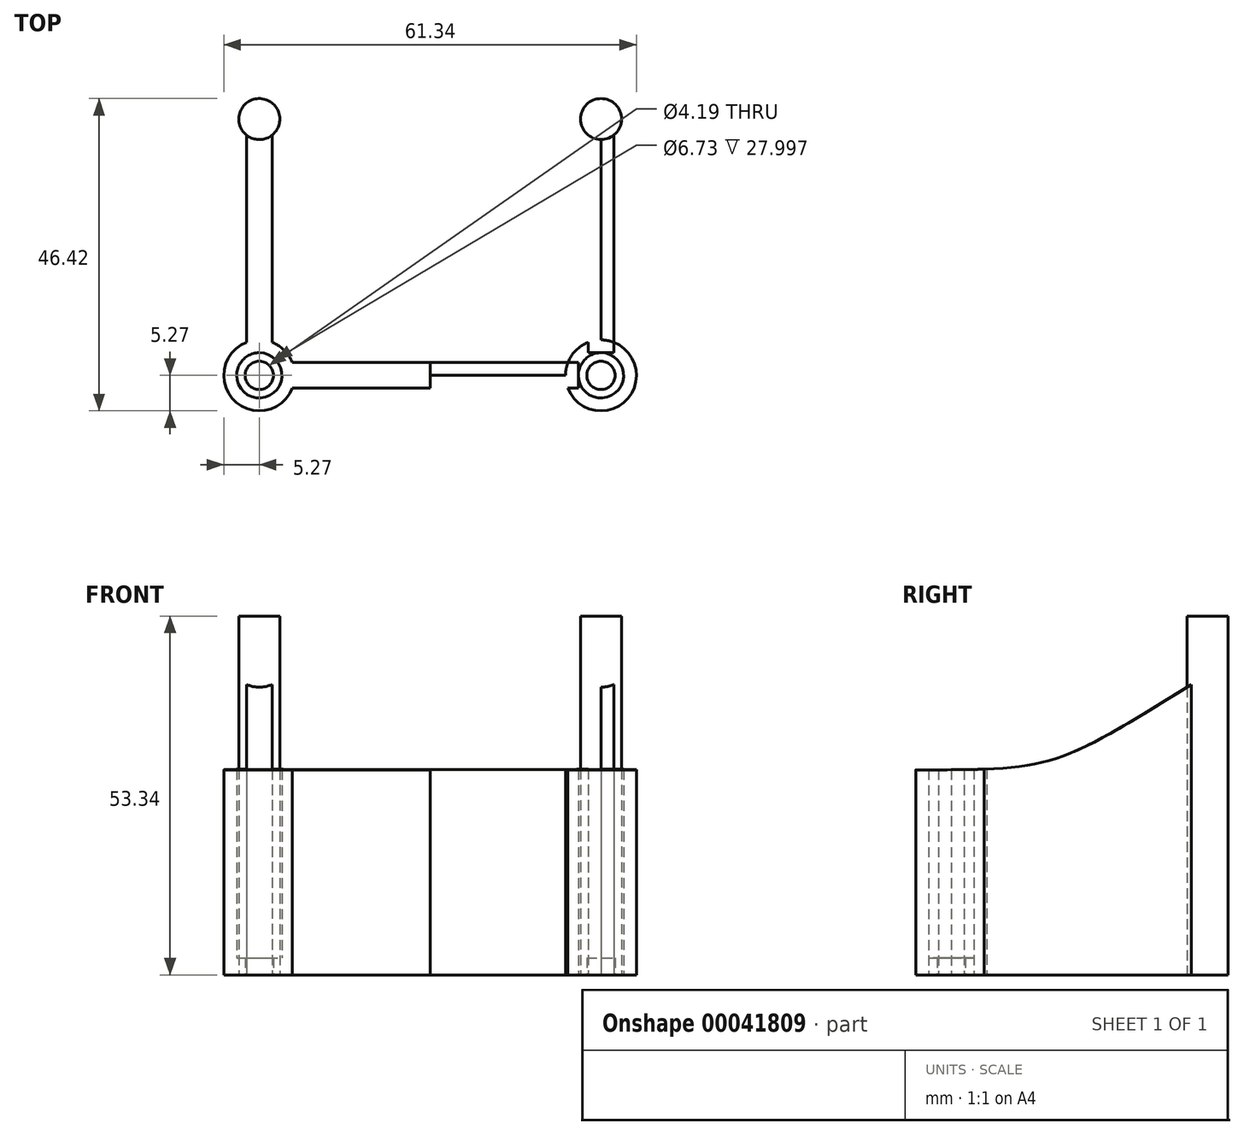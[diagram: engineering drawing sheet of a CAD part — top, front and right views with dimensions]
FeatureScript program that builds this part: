
annotation { "Feature Type Name" : "Feature", "Feature Type Description" : "" }
export const myFeature = defineFeature(function(context is Context, id is Id, definition is map)
    precondition{}
    {
        {
            var Q0;
            Q0=qCreatedBy(makeId("Top.planeOp"),FACE);
            var sketch = newSketch(context, id + "F0", { "sketchPlane" : qUnion([Q0])});
            skCircle(sketch, "E0", {"center": v(-25.4, 38.1) * mm, "radius": 3.05 * mm});
            skCircle(sketch, "E1", {"center": v(-25.4, 0) * mm, "radius": 3.37 * mm});
            skCircle(sketch, "E2", {"center": v(-25.4, 0) * mm, "radius": 5.27 * mm});
            skLineSegment(sketch, "E3.bottom", {"start": v(-27.3, 38.1) * mm, "end": v(-23.5, 38.1) * mm});
            skLineSegment(sketch, "E3.top", {"start": v(-27.3, 3.37) * mm, "end": v(-23.5, 3.37) * mm});
            skLineSegment(sketch, "E3.left", {"start": v(-27.3, 38.1) * mm, "end": v(-27.3, 3.37) * mm});
            skLineSegment(sketch, "E3.right", {"start": v(-23.5, 38.1) * mm, "end": v(-23.5, 3.37) * mm});
            skLineSegment(sketch, "E4", {"start": v(-25.4, 38.1) * mm, "end": v(-25.4, 0) * mm, "construction": true});
            skLineSegment(sketch, "E5.bottom", {"start": v(0, 1.9) * mm, "end": v(-22.03, 1.9) * mm});
            skLineSegment(sketch, "E5.top", {"start": v(0, -1.9) * mm, "end": v(-22.03, -1.9) * mm});
            skLineSegment(sketch, "E5.left", {"start": v(0, 1.9) * mm, "end": v(0, -1.9) * mm});
            skLineSegment(sketch, "E5.right", {"start": v(-22.03, 1.9) * mm, "end": v(-22.03, -1.9) * mm});
            skLineSegment(sketch, "E6", {"start": v(-25.4, 0) * mm, "end": v(0, 0) * mm, "construction": true});
            skLineSegment(sketch, "E7.MirrorCS", {"start": v(22.03, 1.9) * mm, "end": v(22.03, -1.9) * mm});
            skLineSegment(sketch, "E8.MirrorCS", {"start": v(27.3, 38.1) * mm, "end": v(23.5, 38.1) * mm});
            skCircle(sketch, "E9.MirrorC", {"center": v(25.4, 38.1) * mm, "radius": 3.05 * mm});
            skCircle(sketch, "E10.MirrorC", {"center": v(25.4, 0) * mm, "radius": 3.37 * mm});
            skCircle(sketch, "E11.MirrorC", {"center": v(25.4, 0) * mm, "radius": 5.27 * mm});
            skLineSegment(sketch, "E12.MirrorCS", {"start": v(0, -1.9) * mm, "end": v(22.03, -1.9) * mm});
            skLineSegment(sketch, "E13.MirrorCS", {"start": v(0, 1.9) * mm, "end": v(22.03, 1.9) * mm});
            skLineSegment(sketch, "E14.MirrorCS", {"start": v(25.4, 0) * mm, "end": v(0, 0) * mm});
            skLineSegment(sketch, "E15.MirrorCS", {"start": v(25.4, 38.1) * mm, "end": v(25.4, 0) * mm});
            skLineSegment(sketch, "E16.MirrorCS", {"start": v(27.3, 38.1) * mm, "end": v(27.3, 3.37) * mm});
            skLineSegment(sketch, "E17.MirrorCS", {"start": v(23.5, 38.1) * mm, "end": v(23.5, 3.37) * mm});
            skLineSegment(sketch, "E18.MirrorCS", {"start": v(27.3, 3.37) * mm, "end": v(23.5, 3.37) * mm});
            skSolve(sketch);
        }
        {
            var Q0;
            {var subQ5=sQuery(id+"F0.wireOp",EDGE,"E1");var subQ7=sQuery(id+"F0.wireOp",EDGE,"E3.top");var subQ8=makeQuery(id+"F0.imprint","INTERSECT",VERTEX,{"derivedFrom":[subQ5,subQ7]});Q0=makeQuery(id+"F0.imprint","IMPRINT",FACE,{"disambiguationData":[TD([[makeQuery(id+"F0.imprint","IMPRINT",EDGE,{"disambiguationData":[TD([[subQ8,-1.0]])],"derivedFrom":subQ5}),-1.0]])]});}
            var Q1;
            {var subQ3=sQuery(id+"F0.wireOp",EDGE,"E0");var subQ5=sQuery(id+"F0.wireOp",EDGE,"E3.left");var subQ7=makeQuery(id+"F0.imprint","INTERSECT",VERTEX,{"derivedFrom":[subQ3,subQ5]});Q1=makeQuery(id+"F0.imprint","IMPRINT",FACE,{"disambiguationData":[TD([[makeQuery(id+"F0.imprint","IMPRINT",EDGE,{"disambiguationData":[TD([[subQ7,-1.0]])],"derivedFrom":subQ3}),-1.0]])]});}
            var Q2;
            {var subQ0=sQuery(id+"F0.wireOp",EDGE,"E3.right");var subQ1=sQuery(id+"F0.wireOp",EDGE,"E2");var subQ2=makeQuery(id+"F0.imprint","INTERSECT",VERTEX,{"derivedFrom":[subQ1,subQ0]});Q2=makeQuery(id+"F0.imprint","IMPRINT",FACE,{"disambiguationData":[TD([[makeQuery(id+"F0.imprint","IMPRINT",EDGE,{"disambiguationData":[TD([[subQ2,-1.0]])],"derivedFrom":subQ1}),1.0]])]});}
            var Q3;
            {var subQ4=sQuery(id+"F0.wireOp",EDGE,"E2");var subQ6=sQuery(id+"F0.wireOp",EDGE,"E5.bottom");var subQ8=makeQuery(id+"F0.imprint","INTERSECT",VERTEX,{"derivedFrom":[subQ4,subQ6]});Q3=makeQuery(id+"F0.imprint","IMPRINT",FACE,{"disambiguationData":[TD([[makeQuery(id+"F0.imprint","IMPRINT",EDGE,{"disambiguationData":[TD([[subQ8,1.0]])],"derivedFrom":subQ4}),1.0]])]});}
            var Q4;
            {var subQ1=sQuery(id+"F0.wireOp",EDGE,"E1");var subQ7=sQuery(id+"F0.wireOp",EDGE,"E3.top");var subQ8=makeQuery(id+"F0.imprint","INTERSECT",VERTEX,{"derivedFrom":[subQ1,subQ7]});Q4=makeQuery(id+"F0.imprint","IMPRINT",FACE,{"disambiguationData":[TD([[makeQuery(id+"F0.imprint","IMPRINT",EDGE,{"disambiguationData":[TD([[subQ8,1.0]])],"derivedFrom":subQ1}),-1.0]])]});}
            var Q5;
            {var subQ4=sQuery(id+"F0.wireOp",EDGE,"E2");var subQ6=sQuery(id+"F0.wireOp",EDGE,"E5.bottom");var subQ7=makeQuery(id+"F0.imprint","INTERSECT",VERTEX,{"derivedFrom":[subQ4,subQ6]});Q5=makeQuery(id+"F0.imprint","IMPRINT",FACE,{"disambiguationData":[TD([[makeQuery(id+"F0.imprint","IMPRINT",EDGE,{"disambiguationData":[TD([[subQ7,1.0]])],"derivedFrom":subQ4}),-1.0]])]});}
            var Q6;
            {var subQ1=sQuery(id+"F0.wireOp",EDGE,"E11.MirrorC");var subQ5=sQuery(id+"F0.wireOp",EDGE,"E13.MirrorCS");var subQ6=makeQuery(id+"F0.imprint","INTERSECT",VERTEX,{"derivedFrom":[subQ1,subQ5]});Q6=makeQuery(id+"F0.imprint","IMPRINT",FACE,{"disambiguationData":[TD([[makeQuery(id+"F0.imprint","IMPRINT",EDGE,{"disambiguationData":[TD([[subQ6,1.0]])],"derivedFrom":subQ1}),1.0]])]});}
            var Q7;
            {var subQ3=sQuery(id+"F0.wireOp",EDGE,"E11.MirrorC");var subQ5=sQuery(id+"F0.wireOp",EDGE,"E13.MirrorCS");var subQ6=makeQuery(id+"F0.imprint","INTERSECT",VERTEX,{"derivedFrom":[subQ3,subQ5]});Q7=makeQuery(id+"F0.imprint","IMPRINT",FACE,{"disambiguationData":[TD([[makeQuery(id+"F0.imprint","IMPRINT",EDGE,{"disambiguationData":[TD([[subQ6,1.0]])],"derivedFrom":subQ3}),-1.0]])]});}
            var Q8;
            {var subQ3=sQuery(id+"F0.wireOp",EDGE,"E16.MirrorCS");var subQ5=sQuery(id+"F0.wireOp",EDGE,"E11.MirrorC");var subQ6=makeQuery(id+"F0.imprint","INTERSECT",VERTEX,{"derivedFrom":[subQ5,subQ3]});Q8=makeQuery(id+"F0.imprint","IMPRINT",FACE,{"disambiguationData":[TD([[makeQuery(id+"F0.imprint","IMPRINT",EDGE,{"disambiguationData":[TD([[subQ6,-1.0]])],"derivedFrom":subQ5}),-1.0]])]});}
            var Q9;
            {var subQ3=sQuery(id+"F0.wireOp",EDGE,"E11.MirrorC");var subQ5=sQuery(id+"F0.wireOp",EDGE,"E12.MirrorCS");var subQ6=makeQuery(id+"F0.imprint","INTERSECT",VERTEX,{"derivedFrom":[subQ3,subQ5]});Q9=makeQuery(id+"F0.imprint","IMPRINT",FACE,{"disambiguationData":[TD([[makeQuery(id+"F0.imprint","IMPRINT",EDGE,{"disambiguationData":[TD([[subQ6,-1.0]])],"derivedFrom":subQ3}),-1.0]])]});}
            var Q10;
            {var subQ1=sQuery(id+"F0.wireOp",EDGE,"E11.MirrorC");var subQ5=sQuery(id+"F0.wireOp",EDGE,"E12.MirrorCS");var subQ6=makeQuery(id+"F0.imprint","INTERSECT",VERTEX,{"derivedFrom":[subQ1,subQ5]});Q10=makeQuery(id+"F0.imprint","IMPRINT",FACE,{"disambiguationData":[TD([[makeQuery(id+"F0.imprint","IMPRINT",EDGE,{"disambiguationData":[TD([[subQ6,-1.0]])],"derivedFrom":subQ1}),1.0]])]});}
            var Q11;
            {var subQ3=sQuery(id+"F0.wireOp",EDGE,"E16.MirrorCS");var subQ5=sQuery(id+"F0.wireOp",EDGE,"E11.MirrorC");var subQ6=makeQuery(id+"F0.imprint","INTERSECT",VERTEX,{"derivedFrom":[subQ5,subQ3]});Q11=makeQuery(id+"F0.imprint","IMPRINT",FACE,{"disambiguationData":[TD([[makeQuery(id+"F0.imprint","IMPRINT",EDGE,{"disambiguationData":[TD([[subQ6,1.0]])],"derivedFrom":subQ5}),-1.0]])]});}
            var Q12;
            {var subQ3=sQuery(id+"F0.wireOp",EDGE,"E9.MirrorC");var subQ5=sQuery(id+"F0.wireOp",EDGE,"E16.MirrorCS");var subQ7=makeQuery(id+"F0.imprint","INTERSECT",VERTEX,{"derivedFrom":[subQ3,subQ5]});Q12=makeQuery(id+"F0.imprint","IMPRINT",FACE,{"disambiguationData":[TD([[makeQuery(id+"F0.imprint","IMPRINT",EDGE,{"disambiguationData":[TD([[subQ7,-1.0]])],"derivedFrom":subQ3}),1.0]])]});}
            var Q13;
            {var subQ0=sQuery(id+"F0.wireOp",EDGE,"E17.MirrorCS");var subQ3=sQuery(id+"F0.wireOp",EDGE,"E9.MirrorC");var subQ4=makeQuery(id+"F0.imprint","INTERSECT",VERTEX,{"derivedFrom":[subQ3,subQ0]});Q13=makeQuery(id+"F0.imprint","IMPRINT",FACE,{"disambiguationData":[TD([[makeQuery(id+"F0.imprint","IMPRINT",EDGE,{"disambiguationData":[TD([[subQ4,1.0]])],"derivedFrom":subQ3}),1.0]])]});}
            var Q14;
            {var subQ3=sQuery(id+"F0.wireOp",EDGE,"E17.MirrorCS");var subQ5=sQuery(id+"F0.wireOp",EDGE,"E11.MirrorC");var subQ6=makeQuery(id+"F0.imprint","INTERSECT",VERTEX,{"derivedFrom":[subQ5,subQ3]});Q14=makeQuery(id+"F0.imprint","IMPRINT",FACE,{"disambiguationData":[TD([[makeQuery(id+"F0.imprint","IMPRINT",EDGE,{"disambiguationData":[TD([[subQ6,-1.0]])],"derivedFrom":subQ5}),-1.0]])]});}
            var Q15;
            {var subQ5=sQuery(id+"F0.wireOp",EDGE,"E11.MirrorC");var subQ9=sQuery(id+"F0.wireOp",EDGE,"E13.MirrorCS");var subQ11=makeQuery(id+"F0.imprint","INTERSECT",VERTEX,{"derivedFrom":[subQ5,subQ9]});Q15=makeQuery(id+"F0.imprint","IMPRINT",FACE,{"disambiguationData":[TD([[makeQuery(id+"F0.imprint","IMPRINT",EDGE,{"disambiguationData":[TD([[subQ11,-1.0]])],"derivedFrom":subQ5}),-1.0]])]});}
            extrude(context, id + "F1", {"entities" : qUnion([Q0, Q1, Q2, Q3, Q4, Q5, Q6, Q7, Q8, Q9, Q10, Q11, Q12, Q13, Q14, Q15]), "depth" : 50.8 * mm});
        }
        {
            var Q0;
            Q0=qCreatedBy(makeId("Right.planeOp"),FACE);
            var sketch = newSketch(context, id + "F2", { "sketchPlane" : qUnion([Q0])});
            skLineSegment(sketch, "E19.0.0", {"start": v(4.91, 0) * mm, "end": v(35.72, 0) * mm});
            skLineSegment(sketch, "E19.0.1", {"start": v(35.72, 0) * mm, "end": v(35.72, 50.8) * mm});
            skLineSegment(sketch, "E19.0.2", {"start": v(35.72, 50.8) * mm, "end": v(4.91, 50.8) * mm});
            skLineSegment(sketch, "E19.0.3", {"start": v(4.91, 50.8) * mm, "end": v(4.91, 0) * mm});
            skLineSegment(sketch, "E20", {"start": v(-5.27, 0) * mm, "end": v(-5.27, 50.8) * mm});
            skLineSegment(sketch, "E21.0", {"start": v(4.91, 50.8) * mm, "end": v(-5.27, 50.8) * mm});
            skLineSegment(sketch, "E22.bottom", {"start": v(35.72, 0) * mm, "end": v(26.83, 0) * mm});
            skLineSegment(sketch, "E22.top", {"start": v(35.72, 8.26) * mm, "end": v(26.83, 8.26) * mm});
            skLineSegment(sketch, "E22.left", {"start": v(35.72, 0) * mm, "end": v(35.72, 8.26) * mm});
            skLineSegment(sketch, "E22.right", {"start": v(26.83, 0) * mm, "end": v(26.83, 8.26) * mm});
            skFitSpline(sketch, "E23", {"points": [v(-5.27, 30.48) * mm, v(35.72, 43.18) * mm], "startDerivative": vector(61.49, 0) * mm, "endDerivative": vector(61.49, 38.1) * mm});
            skLineSegment(sketch, "E24", {"start": v(-5.27, 30.48) * mm, "end": v(35.72, 30.48) * mm, "construction": true});
            skSolve(sketch);
        }
        {
            var Q0;
            Q0=makeQuery(id+"F2.imprint","IMPRINT",FACE,{"disambiguationData":[TD([[makeQuery(id+"F2.imprint","IMPRINT",EDGE,{"derivedFrom":sQuery(id+"F2.wireOp",EDGE,"E22.bottom")}),-1.0]])]});
            var Q1;
            {var subQ5=sQuery(id+"F2.wireOp",EDGE,"E19.0.2");Q1=makeQuery(id+"F2.imprint","IMPRINT",FACE,{"disambiguationData":[TD([[makeQuery(id+"F2.imprint","IMPRINT",EDGE,{"derivedFrom":subQ5}),1.0]])]});}
            var Q2;
            {var subQ5=sQuery(id+"F2.wireOp",EDGE,"E21.0");Q2=makeQuery(id+"F2.imprint","IMPRINT",FACE,{"disambiguationData":[TD([[makeQuery(id+"F2.imprint","IMPRINT",EDGE,{"derivedFrom":subQ5}),1.0]])]});}
            extrude(context, id + "F3", {"entities" : qUnion([Q0, Q1, Q2]), "operationType" : NewBodyOperationType.REMOVE, "oppositeDirection" : true, "depth" : 76.2 * mm, "symmetric" : true});
        }
        {
            var Q0;
            Q0=makeQuery(id+"F1.opExtrude","CAP_FACE",FACE,{"disambiguationData":[OSD([sQuery(id+"F0.wireOp",EDGE,"E1"),sQuery(id+"F0.wireOp",EDGE,"E2"),sQuery(id+"F0.wireOp",EDGE,"E3.bottom"),sQuery(id+"F0.wireOp",EDGE,"E3.left"),sQuery(id+"F0.wireOp",EDGE,"E3.right"),sQuery(id+"F0.wireOp",EDGE,"E5.bottom"),sQuery(id+"F0.wireOp",EDGE,"E5.top"),sQuery(id+"F0.wireOp",EDGE,"E8.MirrorCS"),sQuery(id+"F0.wireOp",EDGE,"E10.MirrorC"),sQuery(id+"F0.wireOp",EDGE,"E11.MirrorC"),sQuery(id+"F0.wireOp",EDGE,"E12.MirrorCS"),sQuery(id+"F0.wireOp",EDGE,"E13.MirrorCS"),sQuery(id+"F0.wireOp",EDGE,"E16.MirrorCS"),sQuery(id+"F0.wireOp",EDGE,"E17.MirrorCS")])],"isStart":true});
            var sketch = newSketch(context, id + "F4", { "sketchPlane" : qUnion([Q0])});
            skLineSegment(sketch, "E25.0.0", {"start": v(-27.3, -4.91) * mm, "end": v(-27.3, -26.83) * mm});
            skLineSegment(sketch, "E25.0.1", {"start": v(-27.3, -26.83) * mm, "end": v(-23.5, -26.83) * mm});
            skLineSegment(sketch, "E25.0.2", {"start": v(-23.5, -26.83) * mm, "end": v(-23.5, -4.91) * mm});
            skArc(sketch, "E25.0.3", {"start": v(-23.5, -4.91) * mm, "mid": v(-21.67, -3.73) * mm, "end": v(-20.49, -1.9) * mm});
            skLineSegment(sketch, "E25.0.4", {"start": v(-20.49, -1.9) * mm, "end": v(20.49, -1.9) * mm});
            skArc(sketch, "E25.0.5", {"start": v(20.49, -1.9) * mm, "mid": v(21.67, -3.73) * mm, "end": v(23.5, -4.91) * mm});
            skLineSegment(sketch, "E25.0.6", {"start": v(23.5, -4.91) * mm, "end": v(23.5, -26.83) * mm});
            skLineSegment(sketch, "E25.0.7", {"start": v(23.5, -26.83) * mm, "end": v(27.3, -26.83) * mm});
            skLineSegment(sketch, "E25.0.8", {"start": v(27.3, -26.83) * mm, "end": v(27.3, -4.91) * mm});
            skArc(sketch, "E25.0.9", {"start": v(27.3, -4.91) * mm, "mid": v(29.13, 3.73) * mm, "end": v(20.49, 1.9) * mm});
            skLineSegment(sketch, "E25.0.10", {"start": v(20.49, 1.9) * mm, "end": v(-20.49, 1.9) * mm});
            skArc(sketch, "E25.0.11", {"start": v(-20.49, 1.9) * mm, "mid": v(-29.13, 3.73) * mm, "end": v(-27.3, -4.91) * mm});
            skCircle(sketch, "E26", {"center": v(-25.4, 0) * mm, "radius": 2.1 * mm});
            skCircle(sketch, "E27.MirrorC", {"center": v(25.4, 0) * mm, "radius": 2.1 * mm});
            skCircle(sketch, "E28", {"center": v(-25.4, 0) * mm, "radius": 5.27 * mm});
            skCircle(sketch, "E29.MirrorC", {"center": v(25.4, 0) * mm, "radius": 5.27 * mm});
            skSolve(sketch);
        }
        {
            var Q0;
            Q0=makeQuery(id+"F4.imprint","IMPRINT",FACE,{"disambiguationData":[TD([[makeQuery(id+"F4.imprint","IMPRINT",EDGE,{"derivedFrom":makeQuery(id+"F1.opExtrude","CAP_EDGE",EDGE,{"disambiguationData":[OSD([sQuery(id+"F0.wireOp",EDGE,"E1")])],"isStart":true})}),1.0]])]});
            var Q1;
            Q1=makeQuery(id+"F4.imprint","IMPRINT",FACE,{"disambiguationData":[TD([[makeQuery(id+"F4.imprint","IMPRINT",EDGE,{"derivedFrom":sQuery(id+"F4.wireOp",EDGE,"E26")}),-1.0]])]});
            var Q2;
            Q2=makeQuery(id+"F4.imprint","IMPRINT",FACE,{"disambiguationData":[TD([[makeQuery(id+"F4.imprint","IMPRINT",EDGE,{"derivedFrom":makeQuery(id+"F1.opExtrude","CAP_EDGE",EDGE,{"disambiguationData":[OSD([sQuery(id+"F0.wireOp",EDGE,"E10.MirrorC")])],"isStart":true})}),-1.0]])]});
            var Q3;
            Q3=makeQuery(id+"F4.imprint","IMPRINT",FACE,{"disambiguationData":[TD([[makeQuery(id+"F4.imprint","IMPRINT",EDGE,{"derivedFrom":sQuery(id+"F4.wireOp",EDGE,"E27.MirrorC")}),1.0]])]});
            extrude(context, id + "F5", {"entities" : qUnion([Q0, Q1, Q2, Q3]), "operationType" : NewBodyOperationType.ADD, "oppositeDirection" : true, "depth" : 2.54 * mm});
        }
        {
            var Q0;
            {var subQ3=sQuery(id+"F0.wireOp",EDGE,"E3.bottom");Q0=makeQuery(id+"F0.imprint","IMPRINT",FACE,{"disambiguationData":[TD([[makeQuery(id+"F0.imprint","IMPRINT",EDGE,{"derivedFrom":subQ3}),-1.0]])]});}
            var Q1;
            {var subQ3=sQuery(id+"F0.wireOp",EDGE,"E3.bottom");Q1=makeQuery(id+"F0.imprint","IMPRINT",FACE,{"disambiguationData":[TD([[makeQuery(id+"F0.imprint","IMPRINT",EDGE,{"derivedFrom":subQ3}),1.0]])]});}
            var Q2;
            {var subQ3=sQuery(id+"F0.wireOp",EDGE,"E8.MirrorCS");var subQ6=sQuery(id+"F0.wireOp",EDGE,"E16.MirrorCS");var subQ8=makeQuery(id+"F0.imprint","INTERSECT",VERTEX,{"derivedFrom":[subQ3,subQ6]});Q2=makeQuery(id+"F0.imprint","IMPRINT",FACE,{"disambiguationData":[TD([[makeQuery(id+"F0.imprint","IMPRINT",EDGE,{"disambiguationData":[TD([[subQ8,-1.0]])],"derivedFrom":subQ3}),-1.0]])]});}
            var Q3;
            {var subQ0=sQuery(id+"F0.wireOp",EDGE,"E16.MirrorCS");var subQ3=sQuery(id+"F0.wireOp",EDGE,"E8.MirrorCS");var subQ4=makeQuery(id+"F0.imprint","INTERSECT",VERTEX,{"derivedFrom":[subQ3,subQ0]});Q3=makeQuery(id+"F0.imprint","IMPRINT",FACE,{"disambiguationData":[TD([[makeQuery(id+"F0.imprint","IMPRINT",EDGE,{"disambiguationData":[TD([[subQ4,-1.0]])],"derivedFrom":subQ3}),1.0]])]});}
            var Q4;
            {var subQ0=sQuery(id+"F0.wireOp",EDGE,"E17.MirrorCS");var subQ3=sQuery(id+"F0.wireOp",EDGE,"E8.MirrorCS");var subQ4=makeQuery(id+"F0.imprint","INTERSECT",VERTEX,{"derivedFrom":[subQ3,subQ0]});Q4=makeQuery(id+"F0.imprint","IMPRINT",FACE,{"disambiguationData":[TD([[makeQuery(id+"F0.imprint","IMPRINT",EDGE,{"disambiguationData":[TD([[subQ4,1.0]])],"derivedFrom":subQ3}),1.0]])]});}
            extrude(context, id + "F6", {"entities" : qUnion([Q0, Q1, Q2, Q3, Q4]), "operationType" : NewBodyOperationType.ADD, "depth" : 53.34 * mm});
        }
    });
